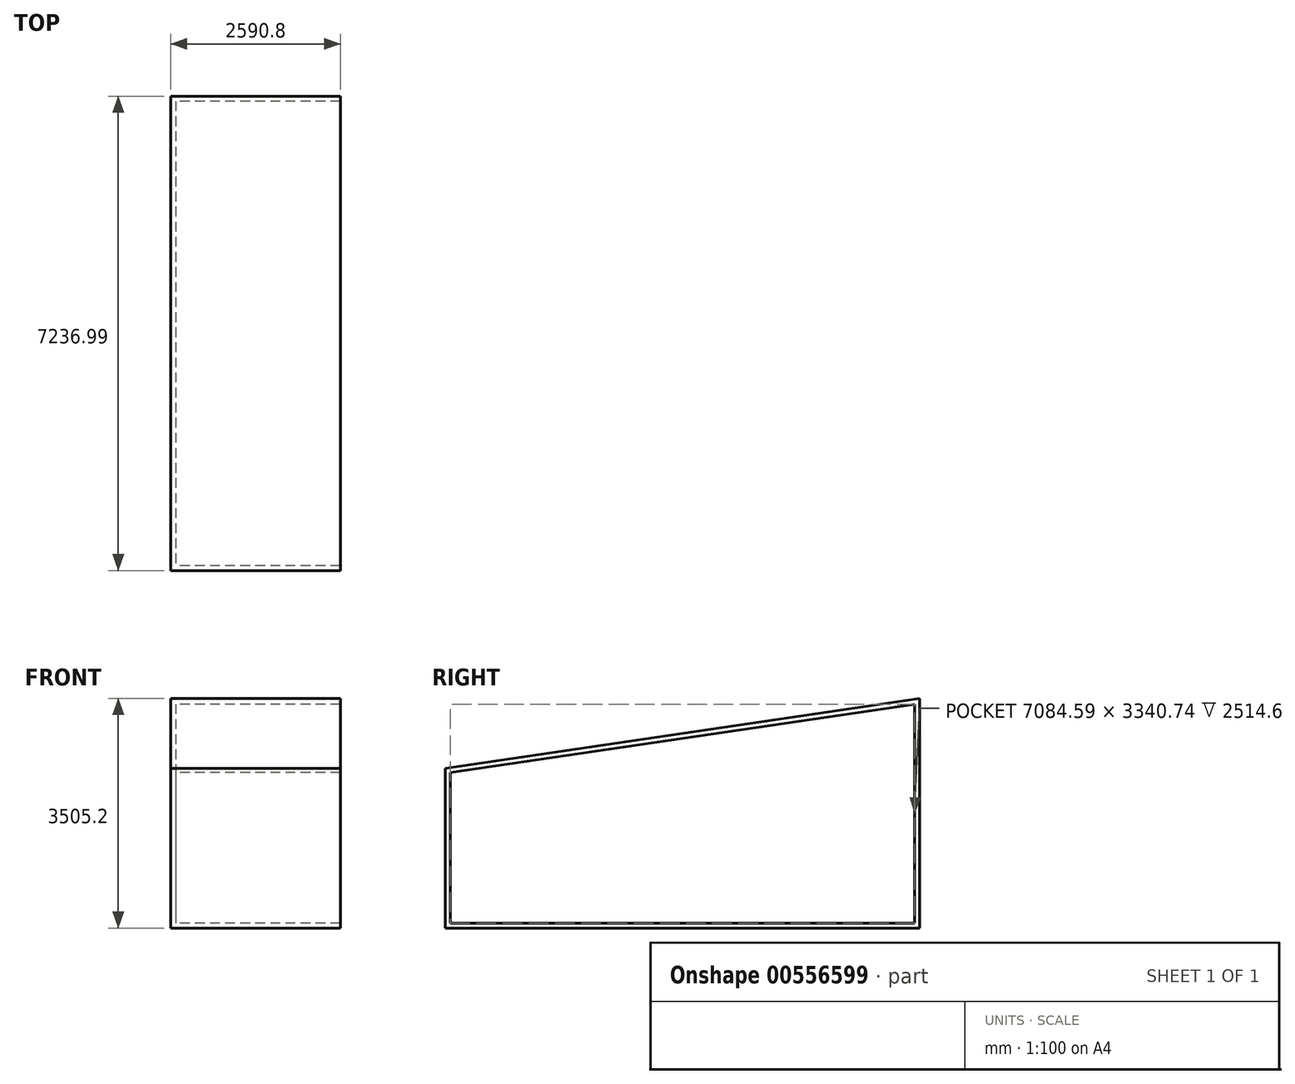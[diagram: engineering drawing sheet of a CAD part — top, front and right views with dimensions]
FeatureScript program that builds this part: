
annotation { "Feature Type Name" : "Feature", "Feature Type Description" : "" }
export const myFeature = defineFeature(function(context is Context, id is Id, definition is map)
    precondition{}
    {
        {
            var Q0;
            Q0=qCreatedBy(makeId("Right.planeOp"),FACE);
            var sketch = newSketch(context, id + "F0", { "sketchPlane" : qUnion([Q0])});
            skLineSegment(sketch, "E0.bottom", {"start": v(3506.24, 3505.2) * mm, "end": v(-3730.75, 2438.4) * mm});
            skLineSegment(sketch, "E0.top", {"start": v(3506.24, 0) * mm, "end": v(-3730.75, 0) * mm});
            skLineSegment(sketch, "E0.left", {"start": v(3506.24, 3505.2) * mm, "end": v(3506.24, 0) * mm});
            skLineSegment(sketch, "E0.right", {"start": v(-3730.75, 2438.4) * mm, "end": v(-3730.75, 0) * mm});
            skLineSegment(sketch, "E1.0", {"start": v(3430.04, 3416.94) * mm, "end": v(-3654.55, 2372.6) * mm});
            skLineSegment(sketch, "E1.1", {"start": v(3430.04, 3416.94) * mm, "end": v(3430.04, 76.2) * mm});
            skLineSegment(sketch, "E1.2", {"start": v(3430.04, 76.2) * mm, "end": v(-3654.55, 76.2) * mm});
            skLineSegment(sketch, "E1.3", {"start": v(-3654.55, 2372.6) * mm, "end": v(-3654.55, 76.2) * mm});
            skSolve(sketch);
        }
        {
            var Q0;
            Q0=makeQuery(id+"F0.imprint","IMPRINT",FACE,{"disambiguationData":[TD([[makeQuery(id+"F0.imprint","IMPRINT",EDGE,{"derivedFrom":sQuery(id+"F0.wireOp",EDGE,"E0.bottom")}),1.0]])]});
            var Q1;
            Q1=sQuery(id+"F0.wireOp",EDGE,"E1.1");
            var Q2;
            Q2=sQuery(id+"F0.wireOp",EDGE,"E1.0");
            var Q3;
            Q3=sQuery(id+"F0.wireOp",EDGE,"E1.3");
            var Q4;
            Q4=sQuery(id+"F0.wireOp",EDGE,"E1.2");
            var Q5;
            Q5=sQuery(id+"F0.wireOp",EDGE,"E0.top");
            var Q6;
            Q6=sQuery(id+"F0.wireOp",EDGE,"E0.right");
            var Q7;
            Q7=sQuery(id+"F0.wireOp",EDGE,"E0.bottom");
            var Q8;
            Q8=sQuery(id+"F0.wireOp",EDGE,"E0.left");
            extrude(context, id + "F1", {"entities" : qUnion([Q0]), "surfaceEntities" : qUnion([Q1, Q2, Q3, Q4, Q5, Q6, Q7, Q8]), "depth" : 2590.8 * mm, "offsetDistance" : 25.4 * mm});
        }
        {
            var Q0;
            Q0=qCreatedBy(makeId("Right.planeOp"),FACE);
            var sketch = newSketch(context, id + "F2", { "sketchPlane" : qUnion([Q0])});
            skLineSegment(sketch, "E2.0", {"start": v(3430.04, 3416.94) * mm, "end": v(-3654.55, 2372.6) * mm});
            skLineSegment(sketch, "E3.0", {"start": v(3430.04, 3416.94) * mm, "end": v(3430.04, 76.2) * mm});
            skLineSegment(sketch, "E4.0", {"start": v(3430.04, 76.2) * mm, "end": v(-3654.55, 76.2) * mm});
            skLineSegment(sketch, "E5.0", {"start": v(-3654.55, 2372.6) * mm, "end": v(-3654.55, 76.2) * mm});
            skSolve(sketch);
        }
        {
            var Q0;
            Q0=makeQuery(id+"F2.imprint","IMPRINT",FACE,{"disambiguationData":[TD([[makeQuery(id+"F2.imprint","IMPRINT",EDGE,{"derivedFrom":sQuery(id+"F2.wireOp",EDGE,"E2.0")}),1.0]])]});
            extrude(context, id + "F3", {"entities" : qUnion([Q0]), "operationType" : NewBodyOperationType.ADD, "depth" : 76.2 * mm, "offsetDistance" : 25.4 * mm});
        }
    });
